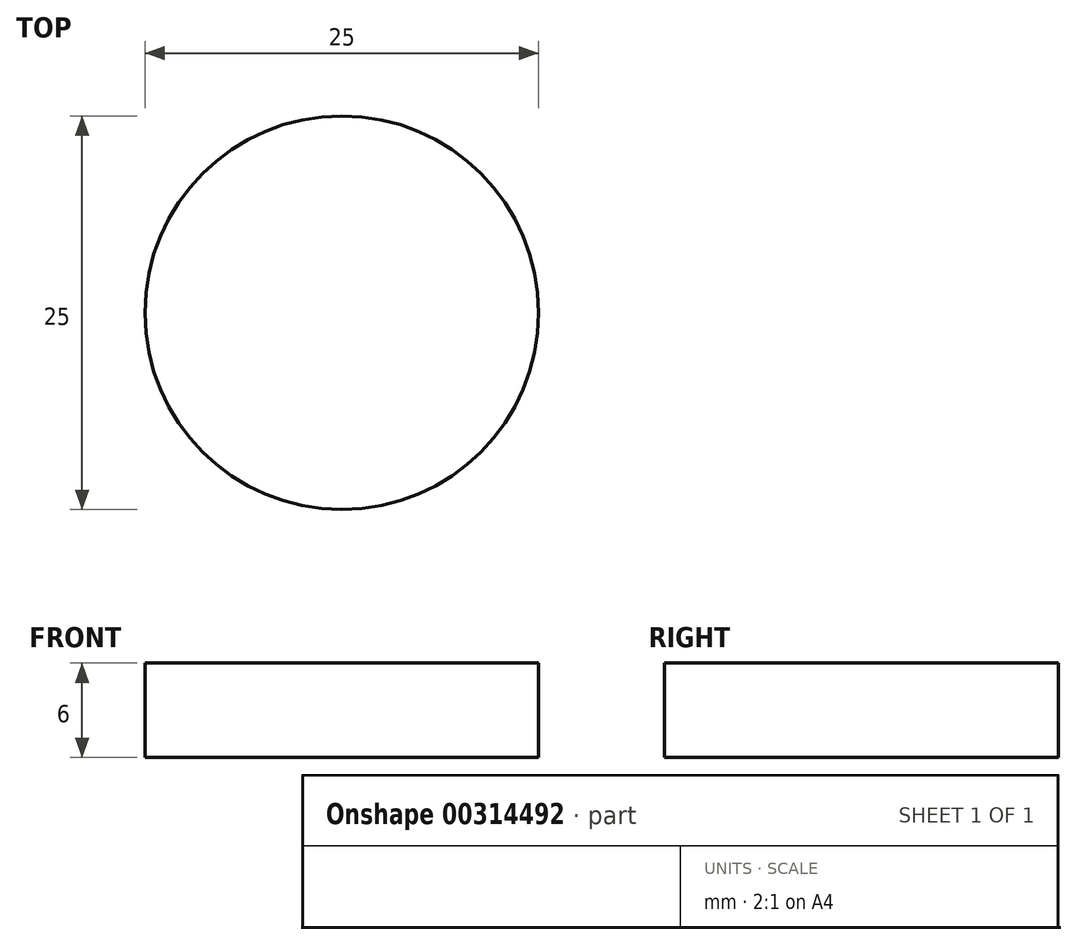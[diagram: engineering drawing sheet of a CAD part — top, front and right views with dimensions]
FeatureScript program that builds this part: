
annotation { "Feature Type Name" : "Feature", "Feature Type Description" : "" }
export const myFeature = defineFeature(function(context is Context, id is Id, definition is map)
    precondition{}
    {
        {
            var Q0;
            Q0=qCreatedBy(makeId("Top.planeOp"),FACE);
            var sketch = newSketch(context, id + "F0", { "sketchPlane" : qUnion([Q0])});
            skCircle(sketch, "E0", {"center": v(-19.25, -5) * mm, "radius": 12.5 * mm});
            skLineSegment(sketch, "E1", {"start": v(-36.35, -19.4) * mm, "end": v(-33.85, -16.9) * mm});
            skLineSegment(sketch, "E2", {"start": v(-34.15, -21.6) * mm, "end": v(-31.65, -19.1) * mm});
            skArc(sketch, "E3", {"start": v(-31.65, -19.1) * mm, "mid": v(-31.65, -16.9) * mm, "end": v(-33.85, -16.9) * mm});
            skArc(sketch, "E4", {"start": v(-36.35, -19.4) * mm, "mid": v(-36.35, -21.6) * mm, "end": v(-34.15, -21.6) * mm});
            skLineSegment(sketch, "E5", {"start": v(-33.85, 6.9) * mm, "end": v(-36.35, 9.4) * mm});
            skLineSegment(sketch, "E6", {"start": v(-31.65, 9.1) * mm, "end": v(-34.15, 11.6) * mm});
            skArc(sketch, "E7", {"start": v(-34.15, 11.6) * mm, "mid": v(-36.35, 11.6) * mm, "end": v(-36.35, 9.4) * mm});
            skArc(sketch, "E8", {"start": v(-33.85, 6.9) * mm, "mid": v(-31.65, 6.9) * mm, "end": v(-31.65, 9.1) * mm});
            skLineSegment(sketch, "E9", {"start": v(-5.35, -21.6) * mm, "end": v(-7.85, -19.1) * mm});
            skLineSegment(sketch, "E10", {"start": v(-3.15, -19.4) * mm, "end": v(-5.65, -16.9) * mm});
            skArc(sketch, "E11", {"start": v(-5.65, -16.9) * mm, "mid": v(-7.85, -16.9) * mm, "end": v(-7.85, -19.1) * mm});
            skArc(sketch, "E12", {"start": v(-5.35, -21.6) * mm, "mid": v(-3.15, -21.6) * mm, "end": v(-3.15, -19.4) * mm});
            skLineSegment(sketch, "E13", {"start": v(-3.15, 9.4) * mm, "end": v(-5.65, 6.9) * mm});
            skLineSegment(sketch, "E14", {"start": v(-5.35, 11.6) * mm, "end": v(-7.85, 9.1) * mm});
            skArc(sketch, "E15", {"start": v(-7.85, 9.1) * mm, "mid": v(-7.85, 6.9) * mm, "end": v(-5.65, 6.9) * mm});
            skArc(sketch, "E16", {"start": v(-3.15, 9.4) * mm, "mid": v(-3.15, 11.6) * mm, "end": v(-5.35, 11.6) * mm});
            skCircle(sketch, "E17", {"center": v(12.8, 5) * mm, "radius": 2.55 * mm});
            skCircle(sketch, "E18", {"center": v(32.8, 5) * mm, "radius": 2.55 * mm});
            skCircle(sketch, "E19", {"center": v(32.8, -5) * mm, "radius": 2.55 * mm});
            skCircle(sketch, "E20", {"center": v(12.8, -5) * mm, "radius": 2.55 * mm});
            skCircle(sketch, "E21", {"center": v(12.8, -15) * mm, "radius": 2.55 * mm});
            skCircle(sketch, "E22", {"center": v(32.8, -15) * mm, "radius": 2.55 * mm});
            skCircle(sketch, "E23", {"center": v(-21, 19.75) * mm, "radius": 1.6 * mm});
            skCircle(sketch, "E24", {"center": v(0, 19.75) * mm, "radius": 1.6 * mm});
            skCircle(sketch, "E25", {"center": v(21, 19.75) * mm, "radius": 1.6 * mm});
            skArc(sketch, "E26", {"start": v(-34.83, 24.75) * mm, "mid": v(-39.2, 22.94) * mm, "end": v(-41, 18.58) * mm});
            skLineSegment(sketch, "E27", {"start": v(34.83, 24.75) * mm, "end": v(-34.83, 24.75) * mm});
            skArc(sketch, "E28", {"start": v(41, 18.58) * mm, "mid": v(39.2, 22.94) * mm, "end": v(34.83, 24.75) * mm});
            skLineSegment(sketch, "E29", {"start": v(-41, -18.58) * mm, "end": v(-41, 18.58) * mm});
            skArc(sketch, "E30", {"start": v(-41, -18.58) * mm, "mid": v(-39.2, -22.94) * mm, "end": v(-34.83, -24.75) * mm});
            skLineSegment(sketch, "E31", {"start": v(39, -24.75) * mm, "end": v(-34.83, -24.75) * mm});
            skLineSegment(sketch, "E32", {"start": v(41, -22.75) * mm, "end": v(41, 18.58) * mm});
            skArc(sketch, "E33", {"start": v(39, -24.75) * mm, "mid": v(40.41, -24.16) * mm, "end": v(41, -22.75) * mm});
            skCircle(sketch, "E34", {"center": v(36.4, -21.75) * mm, "radius": 1.3 * mm});
            skSolve(sketch);
        }
        {
            var Q0;
            Q0=makeQuery(id+"F0.imprint","IMPRINT",FACE,{"disambiguationData":[TD([[makeQuery(id+"F0.imprint","IMPRINT",EDGE,{"derivedFrom":sQuery(id+"F0.wireOp",EDGE,"E0")}),1.0]])]});
            extrude(context, id + "F1", {"entities" : qUnion([Q0]), "depth" : 6 * mm});
        }
    });
